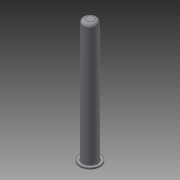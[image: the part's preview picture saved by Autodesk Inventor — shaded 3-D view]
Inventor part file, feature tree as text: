
AUTODESK INVENTOR PART (.ipt)
format: ipt  version: 2014 SP1 (Build 180222100, 222)  size: 107,520 bytes
history: native  units: in
note: dims shown in document units (in); Inventor stores cm internally (conversion verified against a paired STEP export)
features: other x1, revolve x1, fillet x1, shell x1, sketch x1
ambient origin geometry x8: Origin, YZ Plane, XZ Plane, XY Plane, X Axis, Y Axis, Z Axis, Center Point
bodies: Solid1 (feature_tree)
feature tree (5):
  other  "Recoil Spring Guide"
  revolve  "Revolution1"  [1 undecoded]
  fillet  "Fillet1"  Radius=0.0781in
  shell  "Shell1"  Thickness=0.4685in
  sketch  "Sketch1"  dims[d0=0.33in d1=2.893in d2=0.0781in d3=0.4685in d4=0.029in d5=90.0deg d6=0.01in d7=0.028in]
note: 1 required parameter value undecoded (feature->parameter linkage not recoverable at this tier; creation-order binding heuristic only, values carry confidence <= 0.55)
